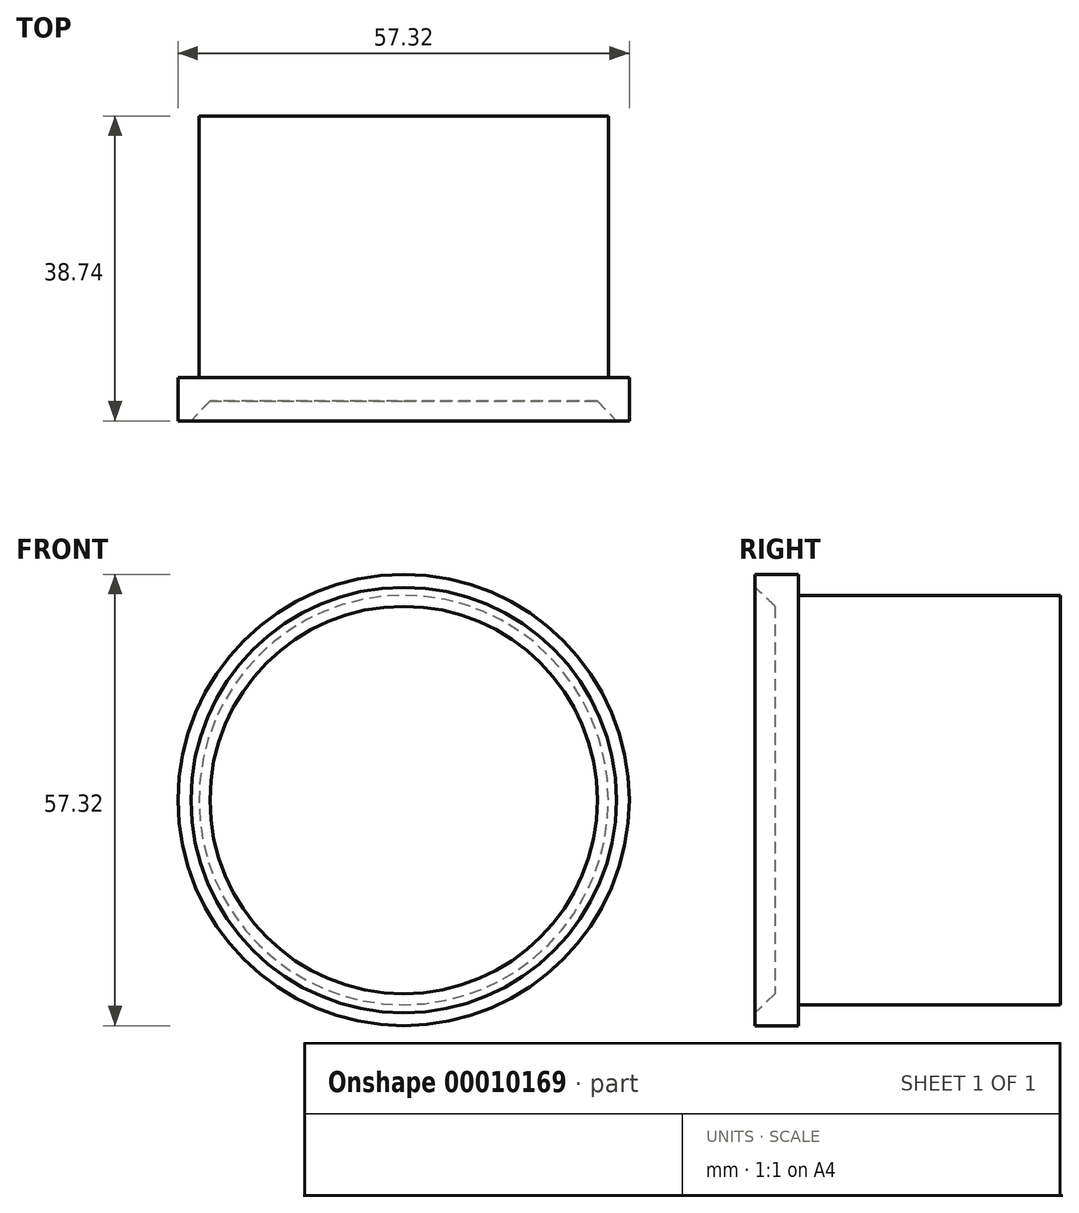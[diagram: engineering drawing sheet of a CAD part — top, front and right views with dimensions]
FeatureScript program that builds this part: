
annotation { "Feature Type Name" : "Feature", "Feature Type Description" : "" }
export const myFeature = defineFeature(function(context is Context, id is Id, definition is map)
    precondition{}
    {
        {
            var Q0;
            Q0=qCreatedBy(makeId("Right.planeOp"),FACE);
            var sketch = newSketch(context, id + "F0", { "sketchPlane" : qUnion([Q0])});
            skLineSegment(sketch, "E0", {"start": v(-2.98, 24.61) * mm, "end": v(-2.98, 0) * mm});
            skLineSegment(sketch, "E1", {"start": v(-2.98, 24.61) * mm, "end": v(-5.52, 27.03) * mm});
            skLineSegment(sketch, "E2", {"start": v(-5.52, 27.03) * mm, "end": v(-5.52, 28.66) * mm});
            skLineSegment(sketch, "E3", {"start": v(-5.52, 28.66) * mm, "end": v(0, 28.66) * mm});
            skLineSegment(sketch, "E4", {"start": v(0, 28.66) * mm, "end": v(0, 26) * mm});
            skLineSegment(sketch, "E5", {"start": v(0, 26) * mm, "end": v(33.22, 26) * mm});
            skLineSegment(sketch, "E6", {"start": v(33.22, 26) * mm, "end": v(33.22, 0) * mm});
            skLineSegment(sketch, "E7", {"start": v(33.22, 0) * mm, "end": v(-2.98, 0) * mm});
            skSolve(sketch);
        }
        {
            var Q0;
            Q0=qSketchRegion(id+"F0",true);
            var Q1;
            Q1=sQuery(id+"F0.wireOp",EDGE,"E7");
            revolve(context, id + "F1", {"entities" : qUnion([Q0]), "axis" : qUnion([Q1]), "revolveType" : RevolveType.FULL});
        }
    });
